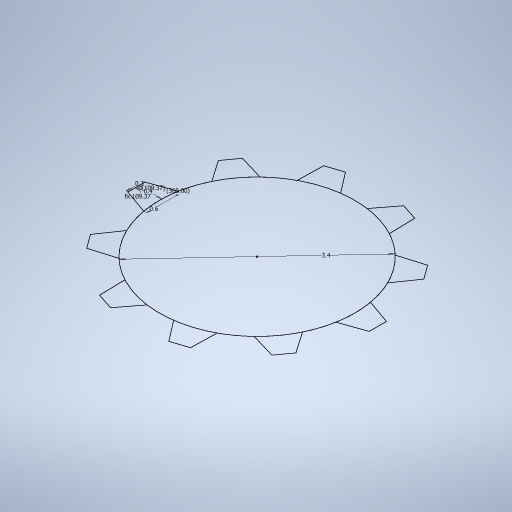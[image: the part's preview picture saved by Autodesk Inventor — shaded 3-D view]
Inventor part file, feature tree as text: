
AUTODESK INVENTOR PART (.ipt)
format: ipt  version: 2023 (Build 270158000, 158)  size: 247,808 bytes
history: native  units: in
note: dims shown in document units (in); Inventor stores cm internally (conversion verified against a paired STEP export)
features: sketch x1
ambient origin geometry x8: Origin, YZ Plane, XZ Plane, XY Plane, X Axis, Y Axis, Z Axis, Center Point
feature tree (1):
  sketch  "Sketch1"  dims[d0=1.3386in d1=0.1181in d2=0.2362in d3=0.1575in d4=0.7515in d5=0.7515in d6=3.937in d8=360.0deg]
